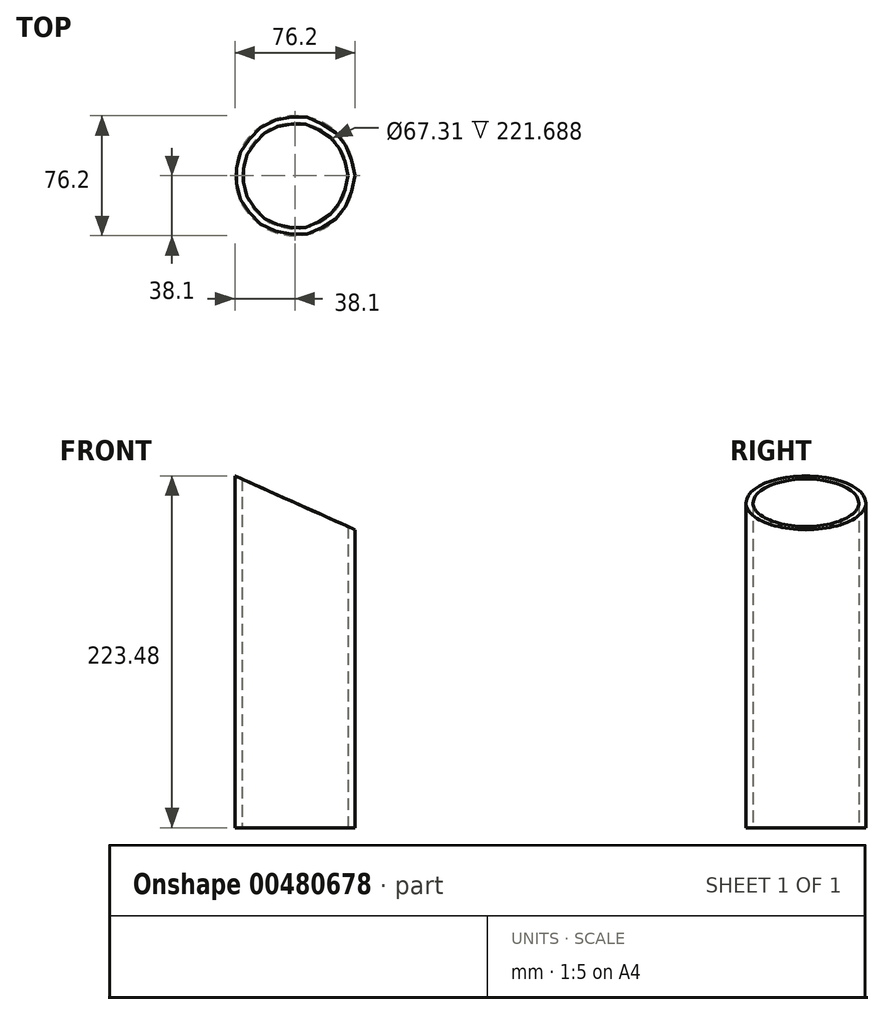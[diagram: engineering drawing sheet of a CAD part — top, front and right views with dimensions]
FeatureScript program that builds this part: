
annotation { "Feature Type Name" : "Feature", "Feature Type Description" : "" }
export const myFeature = defineFeature(function(context is Context, id is Id, definition is map)
    precondition{}
    {
        {
            var Q0;
            Q0=qCreatedBy(makeId("Top.planeOp"),FACE);
            var sketch = newSketch(context, id + "F0", { "sketchPlane" : qUnion([Q0])});
            skCircle(sketch, "E0", {"center": v(0, 0) * mm, "radius": 38.1 * mm});
            skCircle(sketch, "E1", {"center": v(0, 0) * mm, "radius": 33.66 * mm});
            skSolve(sketch);
        }
        {
            var Q0;
            Q0=qSketchRegion(id+"F0",true);
            extrude(context, id + "F1", {"entities" : qUnion([Q0]), "depth" : 254 * mm});
        }
        {
            var Q0;
            Q0=qCreatedBy(makeId("Front.planeOp"),FACE);
            var sketch = newSketch(context, id + "F2", { "sketchPlane" : qUnion([Q0])});
            skLineSegment(sketch, "E2", {"start": v(-122.86, 261.54) * mm, "end": v(52.7, 261.54) * mm});
            skLineSegment(sketch, "E3", {"start": v(52.7, 261.54) * mm, "end": v(52.7, 182.7) * mm});
            skLineSegment(sketch, "E4", {"start": v(52.7, 182.7) * mm, "end": v(-122.86, 261.54) * mm});
            skSolve(sketch);
        }
        {
            var Q0;
            Q0 = qSketchRegion(id + "F2", true);
            extrude(context, id + "F3", {"entities" : qUnion([Q0]), "operationType" : NewBodyOperationType.REMOVE, "oppositeDirection" : true, "depth" : 54.86 * mm, "hasSecondDirection" : true, "secondDirectionOppositeDirection" : false, "secondDirectionDepth" : 56.9 * mm});
        }
    });
